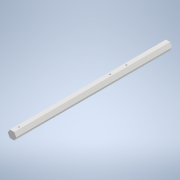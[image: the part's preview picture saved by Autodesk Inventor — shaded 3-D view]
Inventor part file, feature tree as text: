
AUTODESK INVENTOR PART (.ipt)
format: ipt  version: 2022 (Build 260153000, 153)  size: 120,320 bytes
history: native  units: mm
features: extrude x2, sketch x2
ambient origin geometry x8: Origin, YZ Plane, XZ Plane, XY Plane, X Axis, Y Axis, Z Axis, Center Point
bodies: Body1 (feature_tree)
feature tree (4):
  extrude  "Extrusion6"  Depth=3.1mm TaperAngle=360.0deg
  extrude  "Extrusion7"  Depth=115.0mm
  sketch  "Sketch4"  dims[d21=3.1mm d22=60.0mm d24=360.0deg]
  sketch  "Sketch5"  dims[d26=115.0mm d27=0.0mm d28=1.3mm d29=84.1mm d30=72.1mm d31=5.0mm d32=6.0mm d33=0.0mm]
